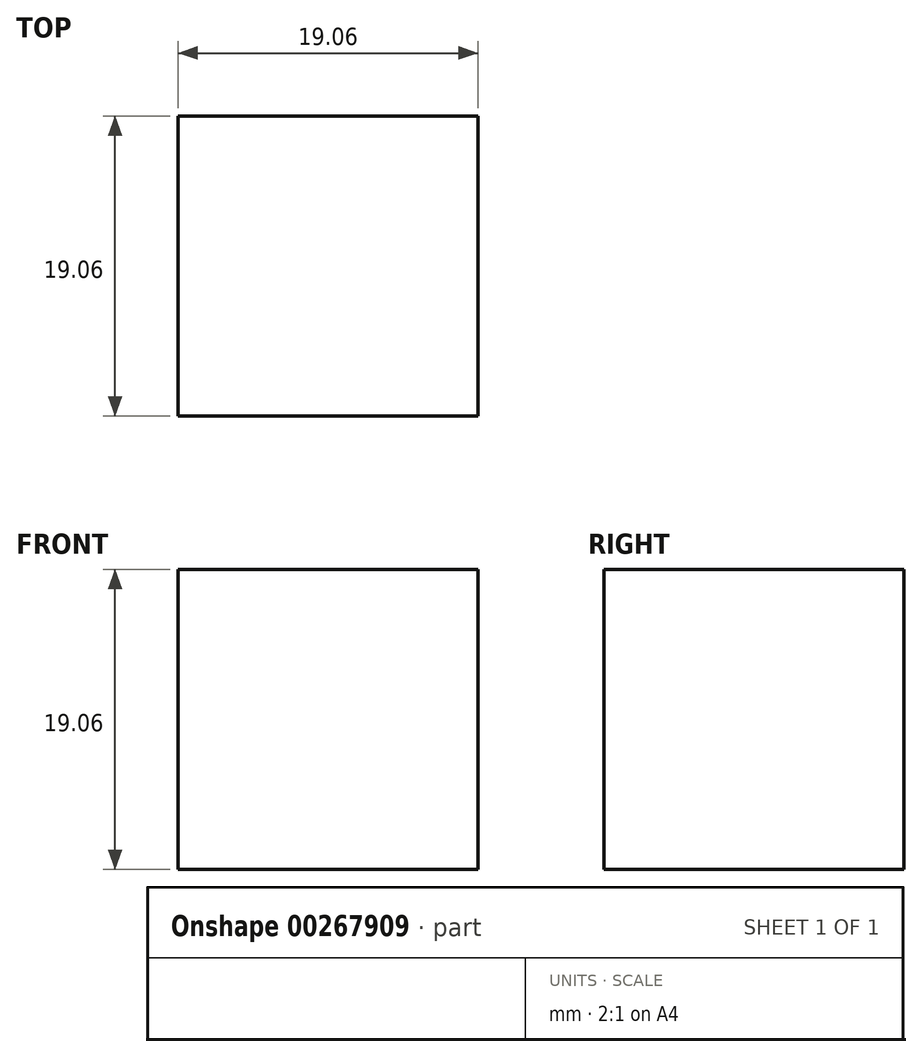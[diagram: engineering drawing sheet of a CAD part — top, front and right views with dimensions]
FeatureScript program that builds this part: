
annotation { "Feature Type Name" : "Feature", "Feature Type Description" : "" }
export const myFeature = defineFeature(function(context is Context, id is Id, definition is map)
    precondition{}
    {
        {
            var Q0;
            Q0=qCreatedBy(makeId("Front.planeOp"),FACE);
            var sketch = newSketch(context, id + "F0", { "sketchPlane" : qUnion([Q0])});
            skLineSegment(sketch, "E0.bottom", {"start": v(-9.52, 9.52) * mm, "end": v(9.53, 9.52) * mm});
            skLineSegment(sketch, "E0.top", {"start": v(-9.53, -9.53) * mm, "end": v(9.53, -9.53) * mm});
            skLineSegment(sketch, "E0.left", {"start": v(-9.52, 9.52) * mm, "end": v(-9.53, -9.53) * mm});
            skLineSegment(sketch, "E0.right", {"start": v(9.53, 9.52) * mm, "end": v(9.53, -9.53) * mm});
            skPoint(sketch, "E0.middle", {"position": v(0, 0) * mm});
            skSolve(sketch);
        }
        {
            var Q0;
            Q0 = qSketchRegion(id + "F0", true);
            extrude(context, id + "F1", {"entities" : qUnion([Q0]), "endBound" : BoundingType.SYMMETRIC, "depth" : 19.05 * mm});
        }
    });
